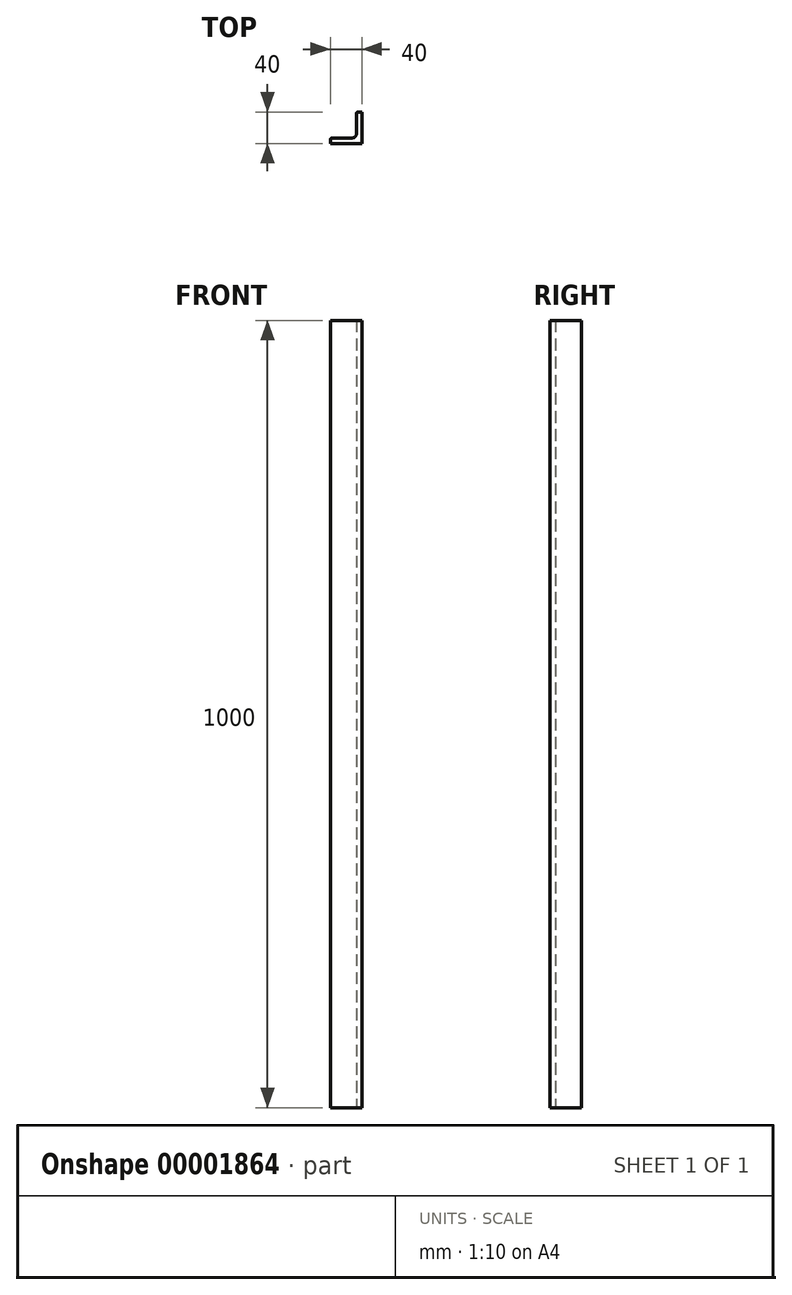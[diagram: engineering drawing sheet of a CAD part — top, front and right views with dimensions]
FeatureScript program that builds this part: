
annotation { "Feature Type Name" : "Feature", "Feature Type Description" : "" }
export const myFeature = defineFeature(function(context is Context, id is Id, definition is map)
    precondition{}
    {
        {
            var Q0;
            Q0=qCreatedBy(makeId("Top.planeOp"),FACE);
            var sketch = newSketch(context, id + "F0", { "sketchPlane" : qUnion([Q0])});
            skLineSegment(sketch, "E0", {"start": v(0, 0) * mm, "end": v(40, 0) * mm});
            skLineSegment(sketch, "E1", {"start": v(40, 0) * mm, "end": v(40, 40) * mm});
            skLineSegment(sketch, "E2", {"start": v(40, 40) * mm, "end": v(35.5, 40) * mm});
            skLineSegment(sketch, "E3", {"start": v(33, 37.5) * mm, "end": v(33, 12) * mm});
            skLineSegment(sketch, "E4", {"start": v(28, 7) * mm, "end": v(2.5, 7) * mm});
            skLineSegment(sketch, "E5", {"start": v(0, 4.5) * mm, "end": v(0, 0) * mm});
            skPoint(sketch, "E6.visualSharp", {"position": v(33, 7) * mm});
            skArc(sketch, "E6.filletArc", {"start": v(28, 7) * mm, "mid": v(31.54, 8.46) * mm, "end": v(33, 12) * mm});
            skPoint(sketch, "E7.visualSharp", {"position": v(33, 40) * mm});
            skArc(sketch, "E7.filletArc", {"start": v(35.5, 40) * mm, "mid": v(33.73, 39.27) * mm, "end": v(33, 37.5) * mm});
            skPoint(sketch, "E8.visualSharp", {"position": v(0, 7) * mm});
            skArc(sketch, "E8.filletArc", {"start": v(2.5, 7) * mm, "mid": v(0.73, 6.27) * mm, "end": v(0, 4.5) * mm});
            skSolve(sketch);
        }
        {
            var Q0;
            Q0 = qSketchRegion(id + "F0", true);
            extrude(context, id + "F1", {"entities" : qUnion([Q0]), "depth" : 1000 * mm});
        }
    });
